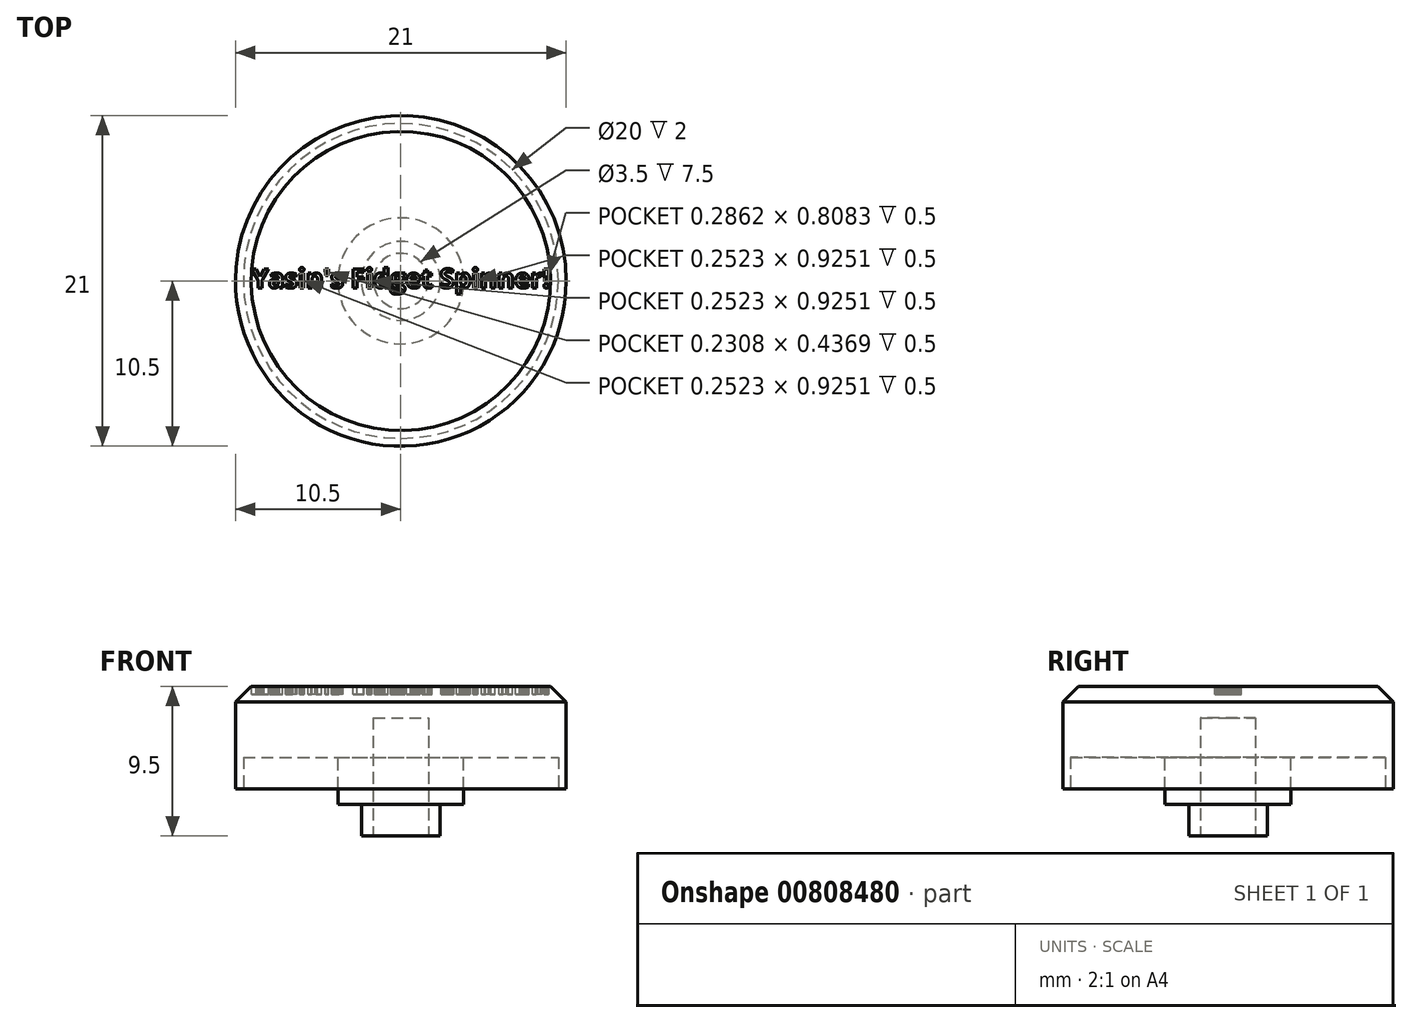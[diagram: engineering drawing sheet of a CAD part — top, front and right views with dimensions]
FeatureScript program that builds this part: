
annotation { "Feature Type Name" : "Feature", "Feature Type Description" : "" }
export const myFeature = defineFeature(function(context is Context, id is Id, definition is map)
    precondition{}
    {
        {
            var Q0;
            Q0=qCreatedBy(makeId("Top.planeOp"),FACE);
            var sketch = newSketch(context, id + "F0", { "sketchPlane" : qUnion([Q0])});
            skCircle(sketch, "E0", {"center": v(0, 0) * mm, "radius": 10.5 * mm});
            skSolve(sketch);
        }
        {
            var Q0;
            Q0=makeQuery(id+"F0.imprint","IMPRINT",FACE,{"disambiguationData":[TD([[makeQuery(id+"F0.imprint","IMPRINT",EDGE,{"derivedFrom":sQuery(id+"F0.wireOp",EDGE,"E0")}),1.0]])]});
            extrude(context, id + "F1", {"entities" : qUnion([Q0]), "depth" : 4 * mm, "offsetDistance" : 25 * mm});
        }
        {
            var Q0;
            Q0=makeQuery(id+"F1.opExtrude","CAP_FACE",FACE,{"disambiguationData":[OSD([sQuery(id+"F0.wireOp",EDGE,"E0")])],"isStart":true});
            var sketch = newSketch(context, id + "F2", { "sketchPlane" : qUnion([Q0])});
            skCircle(sketch, "E1", {"center": v(0, 0) * mm, "radius": 10 * mm});
            skSolve(sketch);
        }
        {
            var Q0;
            Q0=makeQuery(id+"F2.imprint","IMPRINT",FACE,{"disambiguationData":[TD([[makeQuery(id+"F2.imprint","IMPRINT",EDGE,{"derivedFrom":sQuery(id+"F2.wireOp",EDGE,"E1")}),1.0]])]});
            extrude(context, id + "F3", {"entities" : qUnion([Q0]), "operationType" : NewBodyOperationType.REMOVE, "oppositeDirection" : true, "depth" : 2 * mm, "offsetDistance" : 25 * mm});
        }
        {
            var Q0;
            Q0=makeQuery(id+"F3.boolean.opBoolean","COPY",FACE,{"derivedFrom":makeQuery(id+"F3.opExtrude","CAP_FACE",FACE,{"disambiguationData":[OSD([sQuery(id+"F2.wireOp",EDGE,"E1")])],"isStart":false})});
            var sketch = newSketch(context, id + "F4", { "sketchPlane" : qUnion([Q0])});
            skCircle(sketch, "E2", {"center": v(0, 0) * mm, "radius": 4 * mm});
            skCircle(sketch, "E3", {"center": v(0, 0) * mm, "radius": 2.5 * mm});
            skSolve(sketch);
        }
        {
            var Q0;
            Q0=makeQuery(id+"F4.imprint","IMPRINT",FACE,{"disambiguationData":[TD([[makeQuery(id+"F4.imprint","IMPRINT",EDGE,{"derivedFrom":sQuery(id+"F4.wireOp",EDGE,"E2")}),1.0]])]});
            extrude(context, id + "F5", {"entities" : qUnion([Q0]), "operationType" : NewBodyOperationType.ADD, "depth" : 3 * mm, "offsetDistance" : 25 * mm});
        }
        {
            var Q0;
            Q0=makeQuery(id+"F5.boolean.opBoolean","SPLIT",FACE,{"disambiguationData":[TD([makeQuery(id+"F5.opExtrude","SWEPT_FACE",FACE,{"disambiguationData":[OSD([sQuery(id+"F4.wireOp",EDGE,"E3")])]})])],"derivedFrom":makeQuery(id+"F3.boolean.opBoolean","COPY",FACE,{"derivedFrom":makeQuery(id+"F3.opExtrude","CAP_FACE",FACE,{"disambiguationData":[OSD([sQuery(id+"F2.wireOp",EDGE,"E1")])],"isStart":false})})});
            extrude(context, id + "F6", {"entities" : qUnion([Q0]), "operationType" : NewBodyOperationType.ADD, "depth" : 5 * mm, "offsetDistance" : 25 * mm});
        }
        {
            var Q0;
            Q0=makeQuery(id+"F6.opExtrude","CAP_FACE",FACE,{"disambiguationData":[OSD([sQuery(id+"F2.wireOp",EDGE,"E1")])],"isStart":false});
            var sketch = newSketch(context, id + "F7", { "sketchPlane" : qUnion([Q0])});
            skCircle(sketch, "E4", {"center": v(0, 0) * mm, "radius": 1.75 * mm});
            skSolve(sketch);
        }
        {
            var Q0;
            Q0=makeQuery(id+"F1.opExtrude","CAP_FACE",FACE,{"disambiguationData":[OSD([sQuery(id+"F0.wireOp",EDGE,"E0")])],"isStart":false});
            extrude(context, id + "F8", {"entities" : qUnion([Q0]), "operationType" : NewBodyOperationType.ADD, "depth" : 2.5 * mm, "offsetDistance" : 25 * mm});
        }
        {
            var Q0;
            Q0=makeQuery(id+"F7.imprint","IMPRINT",FACE,{"disambiguationData":[TD([[makeQuery(id+"F7.imprint","IMPRINT",EDGE,{"derivedFrom":sQuery(id+"F7.wireOp",EDGE,"E4")}),1.0]])]});
            extrude(context, id + "F9", {"entities" : qUnion([Q0]), "operationType" : NewBodyOperationType.REMOVE, "oppositeDirection" : true, "depth" : 7.5 * mm, "offsetDistance" : 25 * mm});
        }
        {
            var Q0;
            Q0=makeQuery(id+"F8.opExtrude","CAP_EDGE",EDGE,{"disambiguationData":[OSD([sQuery(id+"F0.wireOp",EDGE,"E0")])],"isStart":false});
            chamfer(context, id + "F10", {"entities" : qUnion([Q0]), "width" : 1 * mm, "tangentPropagation" : true});
        }
        {
            var Q0;
            Q0=makeQuery(id+"F8.opExtrude","CAP_FACE",FACE,{"disambiguationData":[OSD([sQuery(id+"F0.wireOp",EDGE,"E0")])],"isStart":false});
            var sketch = newSketch(context, id + "F11", { "sketchPlane" : qUnion([Q0])});
            skText(sketch, "E5", { "text": "Yasin\'s Fidget Spinner!", "fontName": "OpenSans-Bold.ttf"});
            const initialGuessF11  = {"E5": [-0.00947, -0.00044, 1, 0, 0.00122]};
            skSetInitialGuess(sketch, initialGuessF11);
            skSolve(sketch);
        }
        {
            var Q0;
            Q0 = qSketchRegion(id + "F11", true);
            extrude(context, id + "F12", {"entities" : qUnion([Q0]), "operationType" : NewBodyOperationType.REMOVE, "oppositeDirection" : true, "depth" : 0.5 * mm, "offsetDistance" : 25 * mm});
        }
    });
